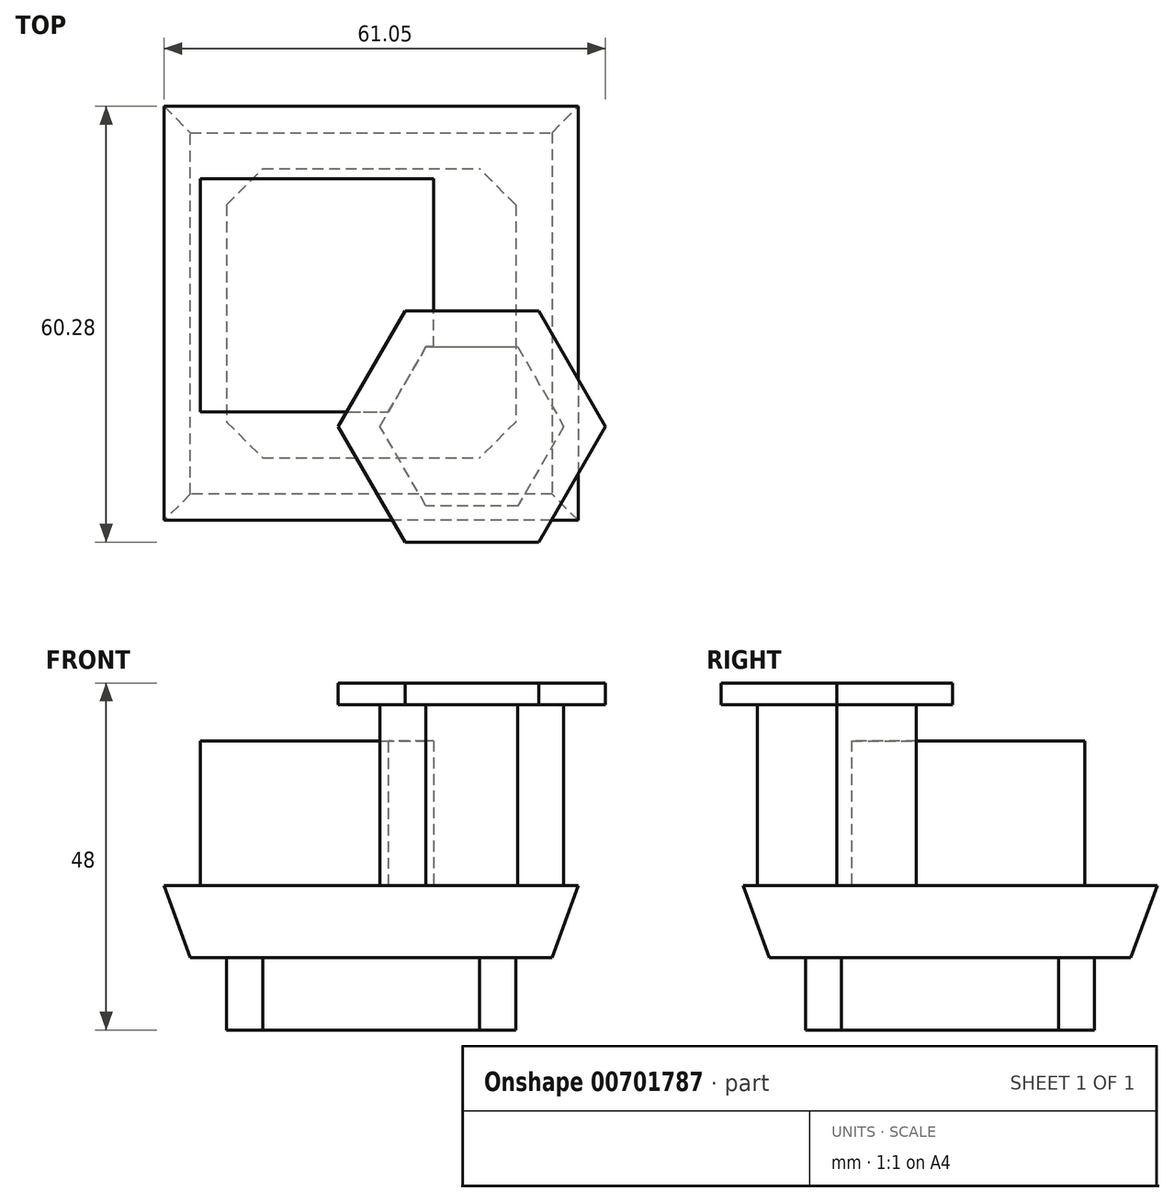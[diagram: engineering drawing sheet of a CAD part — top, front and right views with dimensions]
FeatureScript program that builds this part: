
annotation { "Feature Type Name" : "Feature", "Feature Type Description" : "" }
export const myFeature = defineFeature(function(context is Context, id is Id, definition is map)
    precondition{}
    {
        {
            var Q0;
            Q0=qCreatedBy(makeId("Top.planeOp"),FACE);
            var sketch = newSketch(context, id + "F0", { "sketchPlane" : qUnion([Q0])});
            skLineSegment(sketch, "E0.bottom", {"start": v(-20, 20) * mm, "end": v(20, 20) * mm});
            skLineSegment(sketch, "E0.top", {"start": v(-20, -20) * mm, "end": v(20, -20) * mm});
            skLineSegment(sketch, "E0.left", {"start": v(-20, 20) * mm, "end": v(-20, -20) * mm});
            skLineSegment(sketch, "E0.right", {"start": v(20, 20) * mm, "end": v(20, -20) * mm});
            skSolve(sketch);
        }
        {
            var Q0;
            Q0 = qSketchRegion(id + "F0", true);
            extrude(context, id + "F1", {"entities" : qUnion([Q0]), "depth" : 10 * mm, "offsetDistance" : 25.4 * mm});
        }
        {
            var Q0;
            Q0=makeQuery(id+"F1.opExtrude","SWEPT_EDGE",EDGE,{"disambiguationData":[OSD([sQuery(id+"F0.wireOp",EDGE,"E0.top"),sQuery(id+"F0.wireOp",EDGE,"E0.left")])]});
            var Q1;
            Q1=makeQuery(id+"F1.opExtrude","SWEPT_EDGE",EDGE,{"disambiguationData":[OSD([sQuery(id+"F0.wireOp",EDGE,"E0.bottom"),sQuery(id+"F0.wireOp",EDGE,"E0.left")])]});
            var Q2;
            Q2=makeQuery(id+"F1.opExtrude","SWEPT_EDGE",EDGE,{"disambiguationData":[OSD([sQuery(id+"F0.wireOp",EDGE,"E0.top"),sQuery(id+"F0.wireOp",EDGE,"E0.right")])]});
            var Q3;
            Q3=makeQuery(id+"F1.opExtrude","SWEPT_EDGE",EDGE,{"disambiguationData":[OSD([sQuery(id+"F0.wireOp",EDGE,"E0.bottom"),sQuery(id+"F0.wireOp",EDGE,"E0.right")])]});
            chamfer(context, id + "F2", {"entities" : qUnion([Q0, Q1, Q2, Q3]), "width" : 5 * mm, "tangentPropagation" : true});
        }
        {
            var Q0;
            Q0=makeQuery(id+"F1.opExtrude","CAP_FACE",FACE,{"disambiguationData":[OSD([sQuery(id+"F0.wireOp",EDGE,"E0.bottom"),sQuery(id+"F0.wireOp",EDGE,"E0.top"),sQuery(id+"F0.wireOp",EDGE,"E0.left"),sQuery(id+"F0.wireOp",EDGE,"E0.right")])],"isStart":false});
            var sketch = newSketch(context, id + "F3", { "sketchPlane" : qUnion([Q0])});
            skLineSegment(sketch, "E1.bottom", {"start": v(-25, -25) * mm, "end": v(25, -25) * mm});
            skLineSegment(sketch, "E1.top", {"start": v(-25, 25) * mm, "end": v(25, 25) * mm});
            skLineSegment(sketch, "E1.left", {"start": v(-25, -25) * mm, "end": v(-25, 25) * mm});
            skLineSegment(sketch, "E1.right", {"start": v(25, -25) * mm, "end": v(25, 25) * mm});
            skSolve(sketch);
        }
        {
            var Q0;
            Q0 = qSketchRegion(id + "F3", true);
            extrude(context, id + "F4", {"entities" : qUnion([Q0]), "operationType" : NewBodyOperationType.ADD, "depth" : 10 * mm, "offsetDistance" : 25 * mm, "hasDraft" : true, "draftAngle" : 20 * degree});
        }
        {
            var Q0;
            Q0=makeQuery(id+"F4.opExtrude","CAP_FACE",FACE,{"disambiguationData":[OSD([sQuery(id+"F3.wireOp",EDGE,"E1.bottom"),sQuery(id+"F3.wireOp",EDGE,"E1.top"),sQuery(id+"F3.wireOp",EDGE,"E1.left"),sQuery(id+"F3.wireOp",EDGE,"E1.right")])],"isStart":false});
            var sketch = newSketch(context, id + "F5", { "sketchPlane" : qUnion([Q0])});
            skLineSegment(sketch, "E2.bottom", {"start": v(-23.64, -13.64) * mm, "end": v(8.64, -13.64) * mm});
            skLineSegment(sketch, "E2.top", {"start": v(-23.64, 18.64) * mm, "end": v(8.64, 18.64) * mm});
            skLineSegment(sketch, "E2.left", {"start": v(-23.64, -13.64) * mm, "end": v(-23.64, 18.64) * mm});
            skLineSegment(sketch, "E2.right", {"start": v(8.64, -13.64) * mm, "end": v(8.64, 18.64) * mm});
            skSolve(sketch);
        }
        {
            var Q0;
            Q0 = qSketchRegion(id + "F5", true);
            extrude(context, id + "F6", {"entities" : qUnion([Q0]), "operationType" : NewBodyOperationType.ADD, "depth" : 20 * mm, "offsetDistance" : 25 * mm});
        }
        {
            var Q0;
            Q0=makeQuery(id+"F4.opExtrude","CAP_FACE",FACE,{"disambiguationData":[OSD([sQuery(id+"F3.wireOp",EDGE,"E1.bottom"),sQuery(id+"F3.wireOp",EDGE,"E1.top"),sQuery(id+"F3.wireOp",EDGE,"E1.left"),sQuery(id+"F3.wireOp",EDGE,"E1.right")])],"isStart":false});
            var sketch = newSketch(context, id + "F7", { "sketchPlane" : qUnion([Q0])});
            skCircle(sketch, "E3.cCircle", {"center": v(13.94, -15.64) * mm, "radius": 11 * mm, "construction": true});
            skLineSegment(sketch, "E3.0", {"start": v(26.64, -15.64) * mm, "end": v(20.29, -26.64) * mm});
            skLineSegment(sketch, "E3.1", {"start": v(20.29, -26.64) * mm, "end": v(7.59, -26.64) * mm});
            skLineSegment(sketch, "E3.2", {"start": v(7.59, -26.64) * mm, "end": v(1.24, -15.64) * mm});
            skLineSegment(sketch, "E3.3", {"start": v(1.24, -15.64) * mm, "end": v(7.59, -4.64) * mm});
            skLineSegment(sketch, "E3.4", {"start": v(7.59, -4.64) * mm, "end": v(20.29, -4.64) * mm});
            skLineSegment(sketch, "E3.5", {"start": v(20.29, -4.64) * mm, "end": v(26.64, -15.64) * mm});
            skPoint(sketch, "E3.0.midPoint", {"position": v(23.46, -21.14) * mm});
            skSolve(sketch);
        }
        {
            var Q0;
            Q0 = qSketchRegion(id + "F7", true);
            extrude(context, id + "F8", {"entities" : qUnion([Q0]), "operationType" : NewBodyOperationType.ADD, "depth" : 25 * mm, "offsetDistance" : 25 * mm});
        }
        {
            var Q0;
            Q0=makeQuery(id+"F8.opExtrude","CAP_FACE",FACE,{"disambiguationData":[OSD([sQuery(id+"F7.wireOp",EDGE,"E3.0"),sQuery(id+"F7.wireOp",EDGE,"E3.1"),sQuery(id+"F7.wireOp",EDGE,"E3.2"),sQuery(id+"F7.wireOp",EDGE,"E3.3"),sQuery(id+"F7.wireOp",EDGE,"E3.4"),sQuery(id+"F7.wireOp",EDGE,"E3.5")])],"isStart":false});
            var sketch = newSketch(context, id + "F9", { "sketchPlane" : qUnion([Q0])});
            skLineSegment(sketch, "E4.0", {"start": v(32.41, -15.64) * mm, "end": v(23.18, 0.36) * mm});
            skLineSegment(sketch, "E4.1", {"start": v(4.7, 0.36) * mm, "end": v(-4.54, -15.64) * mm});
            skLineSegment(sketch, "E4.2", {"start": v(-4.54, -15.64) * mm, "end": v(4.7, -31.64) * mm});
            skLineSegment(sketch, "E4.3", {"start": v(23.18, 0.36) * mm, "end": v(4.7, 0.36) * mm});
            skLineSegment(sketch, "E4.4", {"start": v(4.7, -31.64) * mm, "end": v(23.18, -31.64) * mm});
            skLineSegment(sketch, "E4.5", {"start": v(23.18, -31.64) * mm, "end": v(32.41, -15.64) * mm});
            skSolve(sketch);
        }
        {
            var Q0;
            Q0 = qSketchRegion(id + "F9", true);
            extrude(context, id + "F10", {"entities" : qUnion([Q0]), "operationType" : NewBodyOperationType.ADD, "depth" : 3 * mm, "offsetDistance" : 25 * mm});
        }
    });
